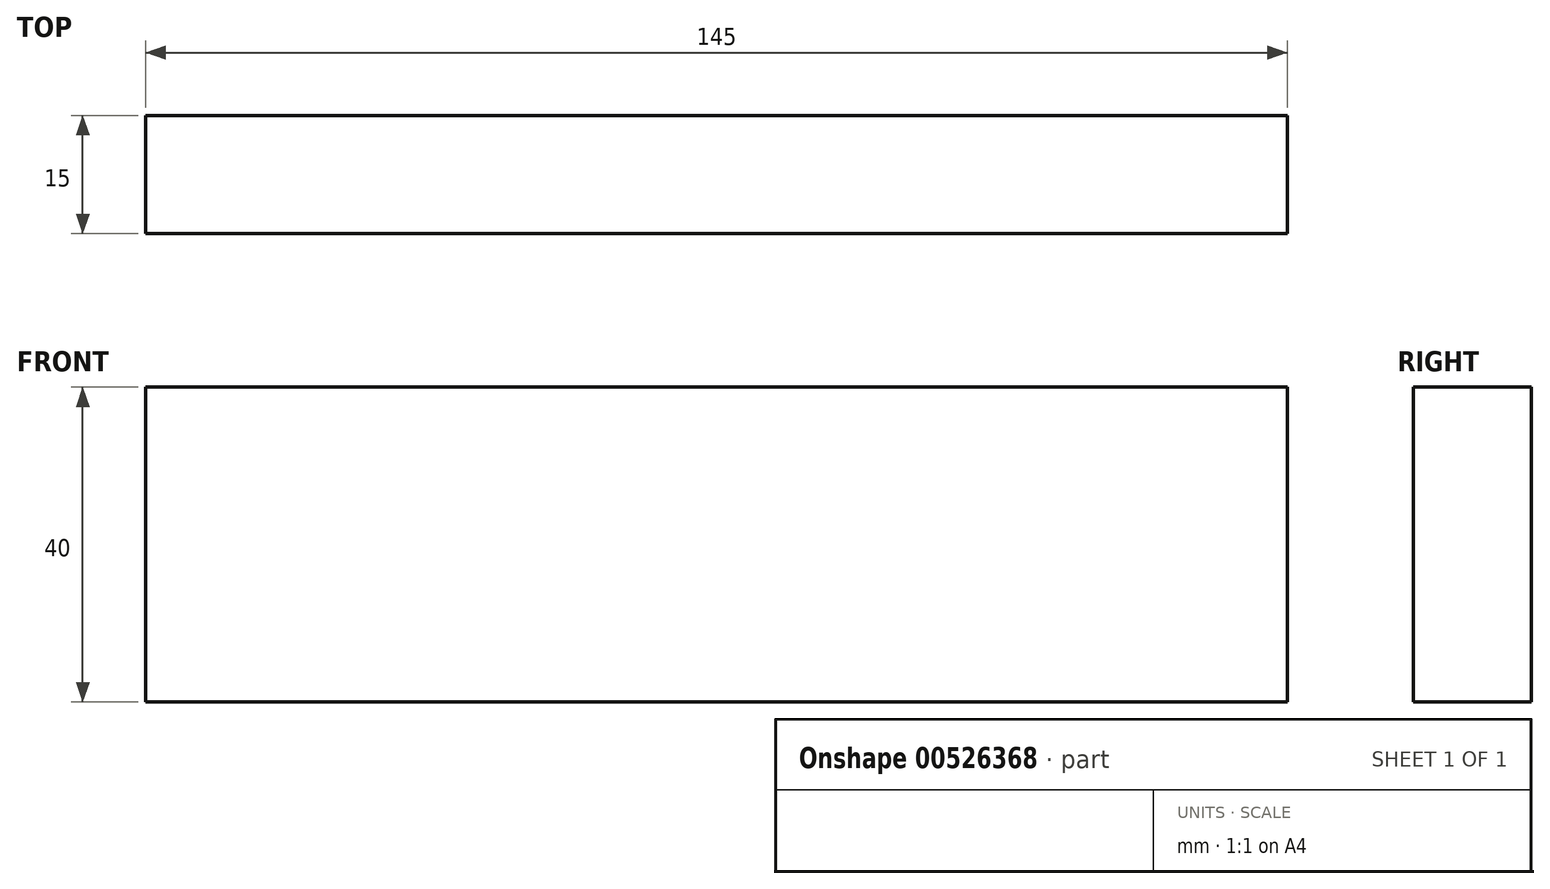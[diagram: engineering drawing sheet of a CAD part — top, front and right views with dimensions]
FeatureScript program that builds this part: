
annotation { "Feature Type Name" : "Feature", "Feature Type Description" : "" }
export const myFeature = defineFeature(function(context is Context, id is Id, definition is map)
    precondition{}
    {
        {
            var Q0;
            Q0=qCreatedBy(makeId("Front.planeOp"),FACE);
            var sketch = newSketch(context, id + "F0", { "sketchPlane" : qUnion([Q0])});
            skLineSegment(sketch, "E0.bottom", {"start": v(0, 0) * mm, "end": v(145, 0) * mm});
            skLineSegment(sketch, "E0.top", {"start": v(0, 40) * mm, "end": v(145, 40) * mm});
            skLineSegment(sketch, "E0.left", {"start": v(0, 0) * mm, "end": v(0, 40) * mm});
            skLineSegment(sketch, "E0.right", {"start": v(145, 0) * mm, "end": v(145, 40) * mm});
            skSolve(sketch);
        }
        {
            var Q0;
            Q0=makeQuery(id+"F0.imprint","IMPRINT",FACE,{"disambiguationData":[TD([[makeQuery(id+"F0.imprint","IMPRINT",EDGE,{"derivedFrom":sQuery(id+"F0.wireOp",EDGE,"E0.bottom")}),1.0]])]});
            extrude(context, id + "F1", {"entities" : qUnion([Q0]), "depth" : 15 * mm, "offsetDistance" : 25 * mm});
        }
    });
